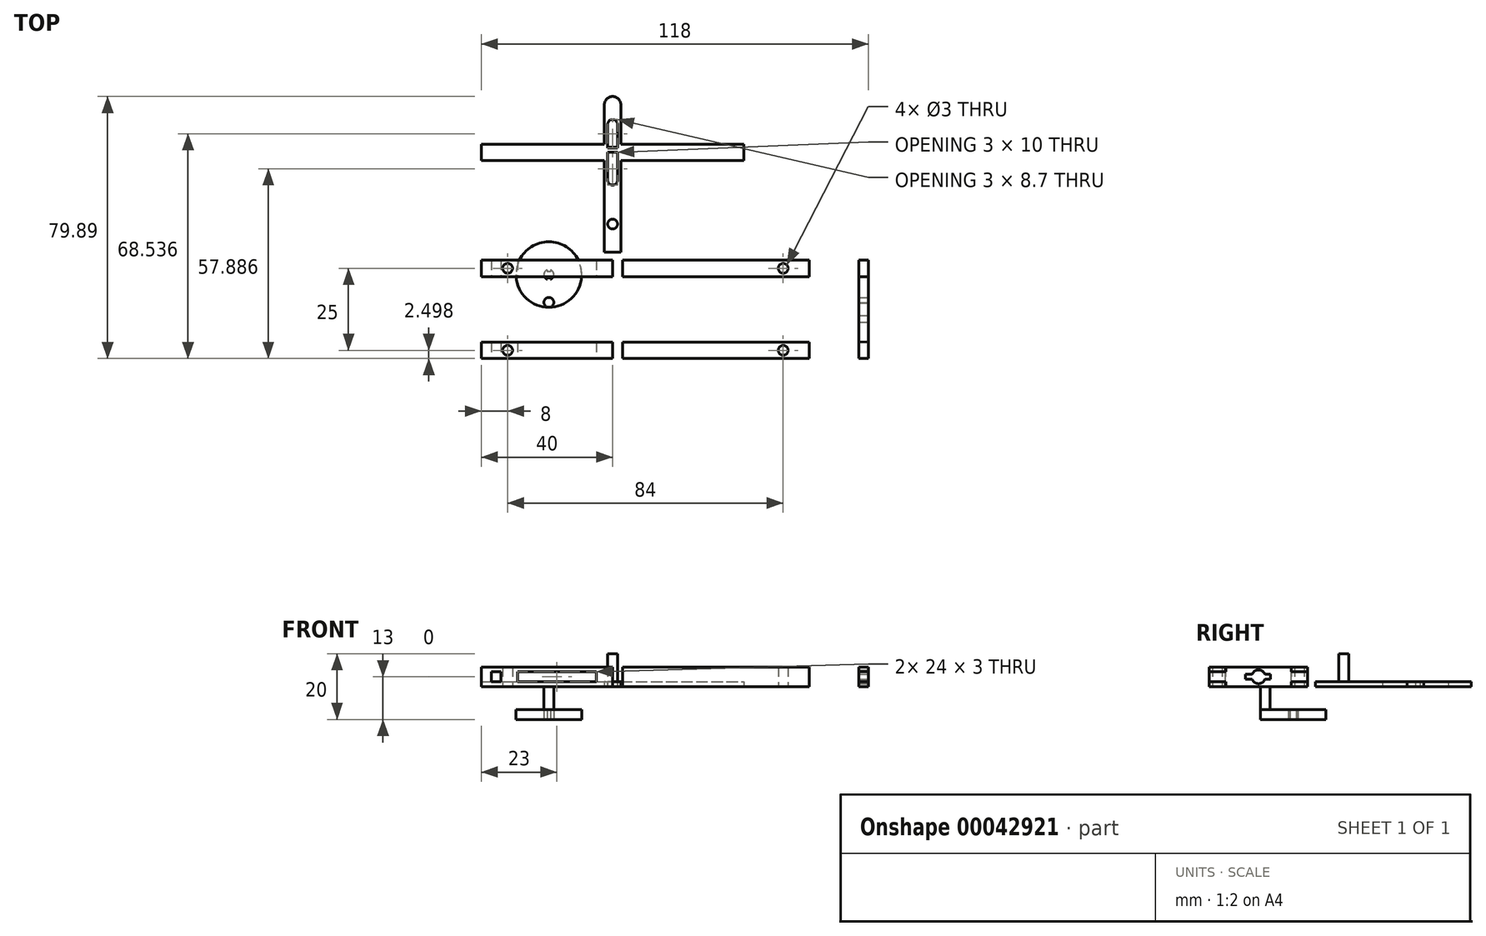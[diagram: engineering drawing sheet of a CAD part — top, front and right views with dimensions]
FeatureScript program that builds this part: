
annotation { "Feature Type Name" : "Feature", "Feature Type Description" : "" }
export const myFeature = defineFeature(function(context is Context, id is Id, definition is map)
    precondition{}
    {
        {
            var Q0;
            Q0=qCreatedBy(makeId("Top.planeOp"),FACE);
            var sketch = newSketch(context, id + "F0", { "sketchPlane" : qUnion([Q0])});
            skLineSegment(sketch, "E0.bottom", {"start": v(-50, 54.04) * mm, "end": v(50, 54.04) * mm});
            skLineSegment(sketch, "E0.top", {"start": v(-50, 49.04) * mm, "end": v(50, 49.04) * mm});
            skLineSegment(sketch, "E0.left", {"start": v(-50, 54.04) * mm, "end": v(-50, 49.04) * mm});
            skLineSegment(sketch, "E0.right", {"start": v(50, 54.04) * mm, "end": v(50, 49.04) * mm});
            skLineSegment(sketch, "E1.bottom", {"start": v(-50, 29.04) * mm, "end": v(50, 29.04) * mm});
            skLineSegment(sketch, "E1.top", {"start": v(-50, 24.04) * mm, "end": v(50, 24.04) * mm});
            skLineSegment(sketch, "E1.left", {"start": v(-50, 29.04) * mm, "end": v(-50, 24.04) * mm});
            skLineSegment(sketch, "E1.right", {"start": v(50, 29.04) * mm, "end": v(50, 24.04) * mm});
            skLineSegment(sketch, "E2", {"start": v(-50, 51.54) * mm, "end": v(50, 51.54) * mm, "construction": true});
            skLineSegment(sketch, "E3", {"start": v(-50, 26.54) * mm, "end": v(50, 26.54) * mm, "construction": true});
            skLineSegment(sketch, "E4", {"start": v(-42, 54.04) * mm, "end": v(-42, 49.04) * mm, "construction": true});
            skLineSegment(sketch, "E5", {"start": v(-42, 29.04) * mm, "end": v(-42, 24.04) * mm, "construction": true});
            skLineSegment(sketch, "E6", {"start": v(42, 29.04) * mm, "end": v(42, 24.04) * mm, "construction": true});
            skLineSegment(sketch, "E7", {"start": v(42, 49.04) * mm, "end": v(42, 54.04) * mm, "construction": true});
            skLineSegment(sketch, "E8", {"start": v(-50, 72.94) * mm, "end": v(-50, -39.34) * mm, "construction": true});
            skCircle(sketch, "E9", {"center": v(-42, 51.54) * mm, "radius": 1.5 * mm});
            skCircle(sketch, "E10", {"center": v(-42, 26.54) * mm, "radius": 1.5 * mm});
            skCircle(sketch, "E11", {"center": v(42, 26.54) * mm, "radius": 1.5 * mm});
            skCircle(sketch, "E12", {"center": v(42, 51.54) * mm, "radius": 1.5 * mm});
            skLineSegment(sketch, "E13.bottom", {"start": v(65, 54.04) * mm, "end": v(68, 54.04) * mm});
            skLineSegment(sketch, "E13.top", {"start": v(65, 24.04) * mm, "end": v(68, 24.04) * mm});
            skLineSegment(sketch, "E13.left", {"start": v(65, 54.04) * mm, "end": v(65, 24.04) * mm});
            skLineSegment(sketch, "E13.right", {"start": v(68, 54.04) * mm, "end": v(68, 24.04) * mm});
            skLineSegment(sketch, "E14", {"start": v(65, 49.04) * mm, "end": v(68, 49.04) * mm});
            skLineSegment(sketch, "E15", {"start": v(65, 29.04) * mm, "end": v(68, 29.17) * mm});
            skLineSegment(sketch, "E16", {"start": v(50, 24.04) * mm, "end": v(81.81, 24.04) * mm, "construction": true});
            skLineSegment(sketch, "E17", {"start": v(50, 54.04) * mm, "end": v(83.42, 54.04) * mm, "construction": true});
            skLineSegment(sketch, "E18.bottom", {"start": v(-10, 54.04) * mm, "end": v(-7, 54.04) * mm});
            skLineSegment(sketch, "E18.top", {"start": v(-10, 49.04) * mm, "end": v(-7, 49.04) * mm});
            skLineSegment(sketch, "E18.left", {"start": v(-10, 54.04) * mm, "end": v(-10, 49.04) * mm});
            skLineSegment(sketch, "E18.right", {"start": v(-7, 54.04) * mm, "end": v(-7, 49.04) * mm});
            skPoint(sketch, "E19.oppositeSnap0", {"position": v(-7, 51.54) * mm});
            skLineSegment(sketch, "E19.bottom", {"start": v(-10, 29.04) * mm, "end": v(-7, 29.04) * mm});
            skLineSegment(sketch, "E19.top", {"start": v(-10, 24.04) * mm, "end": v(-7, 24.04) * mm});
            skLineSegment(sketch, "E19.left", {"start": v(-10, 29.04) * mm, "end": v(-10, 24.04) * mm});
            skLineSegment(sketch, "E19.right", {"start": v(-7, 29.04) * mm, "end": v(-7, 24.04) * mm});
            skLineSegment(sketch, "E20.bottom", {"start": v(-50, 89.43) * mm, "end": v(30, 89.43) * mm});
            skLineSegment(sketch, "E20.top", {"start": v(-50, 84.43) * mm, "end": v(30, 84.43) * mm});
            skLineSegment(sketch, "E20.left", {"start": v(-50, 89.43) * mm, "end": v(-50, 84.43) * mm});
            skLineSegment(sketch, "E20.right", {"start": v(30, 89.43) * mm, "end": v(30, 84.43) * mm});
            skLineSegment(sketch, "E21.bottom", {"start": v(-12.5, 101.43) * mm, "end": v(-7.5, 101.43) * mm});
            skLineSegment(sketch, "E21.top", {"start": v(-12.5, 56.43) * mm, "end": v(-7.5, 56.43) * mm});
            skLineSegment(sketch, "E21.left", {"start": v(-12.5, 101.43) * mm, "end": v(-12.5, 56.43) * mm});
            skLineSegment(sketch, "E21.right", {"start": v(-7.5, 101.43) * mm, "end": v(-7.5, 56.43) * mm});
            skCircle(sketch, "E22", {"center": v(-10, 65.05) * mm, "radius": 1.5 * mm});
            skPoint(sketch, "E22.centerSnap0", {"position": v(-10, 56.43) * mm});
            skLineSegment(sketch, "E23.bottom", {"start": v(-11.5, 95.43) * mm, "end": v(-8.5, 95.43) * mm});
            skLineSegment(sketch, "E23.top", {"start": v(-11.5, 78.43) * mm, "end": v(-8.5, 78.43) * mm});
            skLineSegment(sketch, "E23.left", {"start": v(-11.5, 95.43) * mm, "end": v(-11.5, 78.43) * mm});
            skLineSegment(sketch, "E23.right", {"start": v(-8.5, 95.43) * mm, "end": v(-8.5, 78.43) * mm});
            skArc(sketch, "E24", {"start": v(-8.5, 95.43) * mm, "mid": v(-10, 96.93) * mm, "end": v(-11.5, 95.43) * mm});
            skArc(sketch, "E25", {"start": v(-11.5, 78.43) * mm, "mid": v(-10, 76.93) * mm, "end": v(-8.5, 78.43) * mm});
            skArc(sketch, "E26", {"start": v(-7.5, 101.43) * mm, "mid": v(-10, 103.93) * mm, "end": v(-12.5, 101.43) * mm});
            skLineSegment(sketch, "E27", {"start": v(0, -31.19) * mm, "end": v(0, 115.5) * mm, "construction": true});
            skLineSegment(sketch, "E28", {"start": v(-10, 56.43) * mm, "end": v(-10, 101.43) * mm, "construction": true});
            skCircle(sketch, "E29", {"center": v(-10, 86.93) * mm, "radius": 10 * mm});
            skCircle(sketch, "E30", {"center": v(-10, 95.43) * mm, "radius": 1.5 * mm});
            skLineSegment(sketch, "E31", {"start": v(-50, 86.93) * mm, "end": v(30, 86.93) * mm, "construction": true});
            skSolve(sketch);
        }
        {
            var Q0;
            {var subQ2=sQuery(id+"F0.wireOp",EDGE,"E0.left");Q0=makeQuery(id+"F0.imprint","IMPRINT",FACE,{"disambiguationData":[TD([[makeQuery(id+"F0.imprint","IMPRINT",EDGE,{"derivedFrom":subQ2}),1.0]])]});}
            var Q1;
            Q1=makeQuery(id+"F0.imprint","IMPRINT",FACE,{"disambiguationData":[TD([[makeQuery(id+"F0.imprint","IMPRINT",EDGE,{"derivedFrom":sQuery(id+"F0.wireOp",EDGE,"E18.bottom")}),-1.0]])]});
            var Q2;
            {var subQ2=sQuery(id+"F0.wireOp",EDGE,"E0.right");Q2=makeQuery(id+"F0.imprint","IMPRINT",FACE,{"disambiguationData":[TD([[makeQuery(id+"F0.imprint","IMPRINT",EDGE,{"derivedFrom":subQ2}),-1.0]])]});}
            var Q3;
            {var subQ2=sQuery(id+"F0.wireOp",EDGE,"E1.left");Q3=makeQuery(id+"F0.imprint","IMPRINT",FACE,{"disambiguationData":[TD([[makeQuery(id+"F0.imprint","IMPRINT",EDGE,{"derivedFrom":subQ2}),1.0]])]});}
            var Q4;
            Q4=makeQuery(id+"F0.imprint","IMPRINT",FACE,{"disambiguationData":[TD([[makeQuery(id+"F0.imprint","IMPRINT",EDGE,{"derivedFrom":sQuery(id+"F0.wireOp",EDGE,"E19.bottom")}),-1.0]])]});
            var Q5;
            {var subQ2=sQuery(id+"F0.wireOp",EDGE,"E1.right");Q5=makeQuery(id+"F0.imprint","IMPRINT",FACE,{"disambiguationData":[TD([[makeQuery(id+"F0.imprint","IMPRINT",EDGE,{"derivedFrom":subQ2}),-1.0]])]});}
            extrude(context, id + "F1", {"entities" : qUnion([Q0, Q1, Q2, Q3, Q4, Q5]), "depth" : 6 * mm});
        }
        {
            var Q0;
            {var subQ2=sQuery(id+"F0.wireOp",EDGE,"E13.bottom");Q0=makeQuery(id+"F0.imprint","IMPRINT",FACE,{"disambiguationData":[TD([[makeQuery(id+"F0.imprint","IMPRINT",EDGE,{"derivedFrom":subQ2}),-1.0]])]});}
            var Q1;
            {var subQ1=sQuery(id+"F0.wireOp",EDGE,"E14");Q1=makeQuery(id+"F0.imprint","IMPRINT",FACE,{"disambiguationData":[TD([[makeQuery(id+"F0.imprint","IMPRINT",EDGE,{"derivedFrom":subQ1}),-1.0]])]});}
            var Q2;
            {var subQ2=sQuery(id+"F0.wireOp",EDGE,"E13.top");Q2=makeQuery(id+"F0.imprint","IMPRINT",FACE,{"disambiguationData":[TD([[makeQuery(id+"F0.imprint","IMPRINT",EDGE,{"derivedFrom":subQ2}),1.0]])]});}
            extrude(context, id + "F2", {"entities" : qUnion([Q0, Q1, Q2]), "depth" : 4.5 * mm, "hasSecondDirection" : true, "secondDirectionOppositeDirection" : false, "secondDirectionDepth" : 1.5 * mm});
        }
        {
            var Q0;
            {var subQ1=sQuery(id+"F0.wireOp",EDGE,"E14");Q0=makeQuery(id+"F0.imprint","IMPRINT",FACE,{"disambiguationData":[TD([[makeQuery(id+"F0.imprint","IMPRINT",EDGE,{"derivedFrom":subQ1}),-1.0]])]});}
            extrude(context, id + "F3", {"entities" : qUnion([Q0]), "operationType" : NewBodyOperationType.ADD, "depth" : 6 * mm});
        }
        {
            var Q0;
            {var subQ0=sQuery(id+"F0.wireOp",EDGE,"E13.right");Q0=makeQuery(id+"F3.boolean.opBoolean","MERGE",FACE,{"derivedFrom":[makeQuery(id+"F2.opExtrude","SWEPT_FACE",FACE,{"disambiguationData":[OSD([subQ0])]}),makeQuery(id+"F3.opExtrude","SWEPT_FACE",FACE,{"disambiguationData":[OSD([subQ0])]})]});}
            var sketch = newSketch(context, id + "F4", { "sketchPlane" : qUnion([Q0])});
            skCircle(sketch, "E32", {"center": v(39.1, 3) * mm, "radius": 2.1 * mm});
            skPoint(sketch, "E32.centerSnap0", {"position": v(54.04, 3) * mm});
            skPoint(sketch, "E32.centerSnap1", {"position": v(39.1, 6) * mm});
            skLineSegment(sketch, "E33.bottom", {"start": v(35.1, 3.81) * mm, "end": v(42.69, 3.81) * mm});
            skLineSegment(sketch, "E33.top", {"start": v(35.1, 2.27) * mm, "end": v(42.69, 2.27) * mm});
            skLineSegment(sketch, "E33.left", {"start": v(35.1, 3.81) * mm, "end": v(35.1, 2.27) * mm});
            skLineSegment(sketch, "E33.right", {"start": v(42.69, 3.81) * mm, "end": v(42.69, 2.27) * mm});
            skSolve(sketch);
        }
        {
            var Q0;
            {var subQ0=sQuery(id+"F4.wireOp",EDGE,"E33.bottom");var subQ1=sQuery(id+"F4.wireOp",EDGE,"E32");var subQ3=makeQuery(id+"F4.imprint","INTERSECT",VERTEX,{"disambiguationData":[OD(0.0)],"derivedFrom":[subQ1,subQ0]});Q0=makeQuery(id+"F4.imprint","IMPRINT",FACE,{"disambiguationData":[TD([[makeQuery(id+"F4.imprint","IMPRINT",EDGE,{"disambiguationData":[TD([[subQ3,1.0]])],"derivedFrom":subQ1}),1.0]])]});}
            var Q1;
            {var subQ1=sQuery(id+"F4.wireOp",EDGE,"E32");var subQ4=sQuery(id+"F4.wireOp",EDGE,"E33.bottom");var subQ6=makeQuery(id+"F4.imprint","INTERSECT",VERTEX,{"disambiguationData":[OD(0.0)],"derivedFrom":[subQ1,subQ4]});Q1=makeQuery(id+"F4.imprint","IMPRINT",FACE,{"disambiguationData":[TD([[makeQuery(id+"F4.imprint","IMPRINT",EDGE,{"disambiguationData":[TD([[subQ6,-1.0]])],"derivedFrom":subQ1}),1.0]])]});}
            var Q2;
            {var subQ0=sQuery(id+"F4.wireOp",EDGE,"E33.right");Q2=makeQuery(id+"F4.imprint","IMPRINT",FACE,{"disambiguationData":[TD([[makeQuery(id+"F4.imprint","IMPRINT",EDGE,{"derivedFrom":subQ0}),-1.0]])]});}
            var Q3;
            {var subQ0=sQuery(id+"F4.wireOp",EDGE,"E33.top");var subQ1=sQuery(id+"F4.wireOp",EDGE,"E32");var subQ3=makeQuery(id+"F4.imprint","INTERSECT",VERTEX,{"disambiguationData":[OD(0.0)],"derivedFrom":[subQ1,subQ0]});Q3=makeQuery(id+"F4.imprint","IMPRINT",FACE,{"disambiguationData":[TD([[makeQuery(id+"F4.imprint","IMPRINT",EDGE,{"disambiguationData":[TD([[subQ3,-1.0]])],"derivedFrom":subQ1}),1.0]])]});}
            var Q4;
            {var subQ0=sQuery(id+"F4.wireOp",EDGE,"E33.left");Q4=makeQuery(id+"F4.imprint","IMPRINT",FACE,{"disambiguationData":[TD([[makeQuery(id+"F4.imprint","IMPRINT",EDGE,{"derivedFrom":subQ0}),1.0]])]});}
            extrude(context, id + "F5", {"entities" : qUnion([Q0, Q1, Q2, Q3, Q4]), "operationType" : NewBodyOperationType.REMOVE, "endBound" : BoundingType.THROUGH_ALL, "oppositeDirection" : true, "depth" : 3 * mm});
        }
        {
            var Q0;
            Q0=makeQuery(id+"F1.opExtrude","SWEPT_FACE",FACE,{"disambiguationData":[OSD([sQuery(id+"F0.wireOp",EDGE,"E1.top"),sQuery(id+"F0.wireOp",EDGE,"E19.top")])]});
            var sketch = newSketch(context, id + "F6", { "sketchPlane" : qUnion([Q0])});
            skLineSegment(sketch, "E34.bottom", {"start": v(-7, 4.5) * mm, "end": v(-10, 4.5) * mm});
            skLineSegment(sketch, "E34.top", {"start": v(-7, 1.5) * mm, "end": v(-10, 1.5) * mm});
            skLineSegment(sketch, "E34.left", {"start": v(-7, 1.5) * mm, "end": v(-7, 4.5) * mm});
            skLineSegment(sketch, "E34.right", {"start": v(-10, 1.5) * mm, "end": v(-10, 4.5) * mm});
            skLineSegment(sketch, "E35", {"start": v(-7, 1.5) * mm, "end": v(-7, 4.5) * mm, "construction": true});
            skPoint(sketch, "E36.orphan", {"position": v(-7, 6) * mm});
            skPoint(sketch, "E37.orphan", {"position": v(-10, 6) * mm});
            skPoint(sketch, "E38.orphan", {"position": v(-10, 0) * mm});
            skLineSegment(sketch, "E39.bottom", {"start": v(-47, 4.5) * mm, "end": v(-44, 4.5) * mm});
            skLineSegment(sketch, "E39.top", {"start": v(-47, 1.5) * mm, "end": v(-44, 1.5) * mm});
            skLineSegment(sketch, "E39.left", {"start": v(-47, 4.5) * mm, "end": v(-47, 1.5) * mm});
            skLineSegment(sketch, "E39.right", {"start": v(-44, 4.5) * mm, "end": v(-44, 1.5) * mm});
            skLineSegment(sketch, "E40.bottom", {"start": v(-39, 4.5) * mm, "end": v(-15, 4.5) * mm});
            skLineSegment(sketch, "E40.top", {"start": v(-39, 1.5) * mm, "end": v(-15, 1.5) * mm});
            skLineSegment(sketch, "E40.left", {"start": v(-39, 4.5) * mm, "end": v(-39, 1.5) * mm});
            skLineSegment(sketch, "E40.right", {"start": v(-15, 4.5) * mm, "end": v(-15, 1.5) * mm});
            skSolve(sketch);
        }
        {
            var Q0;
            {var subQ2=sQuery(id+"F6.wireOp",EDGE,"E34.bottom");Q0=makeQuery(id+"F6.imprint","IMPRINT",FACE,{"disambiguationData":[TD([[makeQuery(id+"F6.imprint","IMPRINT",EDGE,{"derivedFrom":subQ2}),1.0]])]});}
            var Q1;
            Q1=makeQuery(id+"F6.imprint","IMPRINT",FACE,{"disambiguationData":[TD([[makeQuery(id+"F6.imprint","IMPRINT",EDGE,{"derivedFrom":sQuery(id+"F6.wireOp",EDGE,"E39.bottom")}),-1.0]])]});
            var Q2;
            Q2=makeQuery(id+"F6.imprint","IMPRINT",FACE,{"disambiguationData":[TD([[makeQuery(id+"F6.imprint","IMPRINT",EDGE,{"derivedFrom":sQuery(id+"F6.wireOp",EDGE,"E40.bottom")}),-1.0]])]});
            extrude(context, id + "F7", {"entities" : qUnion([Q0, Q1, Q2]), "operationType" : NewBodyOperationType.REMOVE, "endBound" : BoundingType.THROUGH_ALL, "oppositeDirection" : true, "depth" : 25 * mm});
        }
        {
            var Q0;
            {var subQ0=sQuery(id+"F0.wireOp",EDGE,"E20.right");Q0=makeQuery(id+"F0.imprint","IMPRINT",FACE,{"disambiguationData":[TD([[makeQuery(id+"F0.imprint","IMPRINT",EDGE,{"derivedFrom":subQ0}),-1.0]])]});}
            var Q1;
            {var subQ0=sQuery(id+"F0.wireOp",EDGE,"E20.left");Q1=makeQuery(id+"F0.imprint","IMPRINT",FACE,{"disambiguationData":[TD([[makeQuery(id+"F0.imprint","IMPRINT",EDGE,{"derivedFrom":subQ0}),1.0]])]});}
            var Q2;
            Q2=makeQuery(id+"F0.imprint","IMPRINT",FACE,{"disambiguationData":[TD([[makeQuery(id+"F0.imprint","IMPRINT",EDGE,{"derivedFrom":sQuery(id+"F0.wireOp",EDGE,"E21.bottom")}),1.0]])]});
            var Q3;
            {var subQ7=sQuery(id+"F0.wireOp",EDGE,"E21.bottom");Q3=makeQuery(id+"F0.imprint","IMPRINT",FACE,{"disambiguationData":[TD([[makeQuery(id+"F0.imprint","IMPRINT",EDGE,{"derivedFrom":subQ7}),-1.0]])]});}
            var Q4;
            {var subQ7=sQuery(id+"F0.wireOp",EDGE,"E21.top");Q4=makeQuery(id+"F0.imprint","IMPRINT",FACE,{"disambiguationData":[TD([[makeQuery(id+"F0.imprint","IMPRINT",EDGE,{"derivedFrom":subQ7}),1.0]])]});}
            var Q5;
            {var subQ3=sQuery(id+"F0.wireOp",EDGE,"E20.bottom");var subQ5=sQuery(id+"F0.wireOp",EDGE,"E21.left");var subQ7=makeQuery(id+"F0.imprint","INTERSECT",VERTEX,{"derivedFrom":[subQ3,subQ5]});Q5=makeQuery(id+"F0.imprint","IMPRINT",FACE,{"disambiguationData":[TD([[makeQuery(id+"F0.imprint","IMPRINT",EDGE,{"disambiguationData":[TD([[subQ7,-1.0]])],"derivedFrom":subQ3}),-1.0]])]});}
            var Q6;
            {var subQ3=sQuery(id+"F0.wireOp",EDGE,"E20.bottom");var subQ5=sQuery(id+"F0.wireOp",EDGE,"E21.right");var subQ7=makeQuery(id+"F0.imprint","INTERSECT",VERTEX,{"derivedFrom":[subQ3,subQ5]});Q6=makeQuery(id+"F0.imprint","IMPRINT",FACE,{"disambiguationData":[TD([[makeQuery(id+"F0.imprint","IMPRINT",EDGE,{"disambiguationData":[TD([[subQ7,1.0]])],"derivedFrom":subQ3}),-1.0]])]});}
            var Q7;
            {var subQ3=sQuery(id+"F0.wireOp",EDGE,"E20.bottom");var subQ5=sQuery(id+"F0.wireOp",EDGE,"E29");var subQ7=makeQuery(id+"F0.imprint","INTERSECT",VERTEX,{"disambiguationData":[OD(0.0)],"derivedFrom":[subQ3,subQ5]});Q7=makeQuery(id+"F0.imprint","IMPRINT",FACE,{"disambiguationData":[TD([[makeQuery(id+"F0.imprint","IMPRINT",EDGE,{"disambiguationData":[TD([[subQ7,-1.0]])],"derivedFrom":subQ3}),-1.0]])]});}
            var Q8;
            {var subQ3=sQuery(id+"F0.wireOp",EDGE,"E20.bottom");var subQ5=sQuery(id+"F0.wireOp",EDGE,"E29");var subQ7=makeQuery(id+"F0.imprint","INTERSECT",VERTEX,{"disambiguationData":[OD(1.0)],"derivedFrom":[subQ3,subQ5]});Q8=makeQuery(id+"F0.imprint","IMPRINT",FACE,{"disambiguationData":[TD([[makeQuery(id+"F0.imprint","IMPRINT",EDGE,{"disambiguationData":[TD([[subQ7,1.0]])],"derivedFrom":subQ3}),-1.0]])]});}
            var Q9;
            {var subQ5=sQuery(id+"F0.wireOp",EDGE,"E20.bottom");var subQ7=sQuery(id+"F0.wireOp",EDGE,"E21.left");var subQ8=makeQuery(id+"F0.imprint","INTERSECT",VERTEX,{"derivedFrom":[subQ5,subQ7]});Q9=makeQuery(id+"F0.imprint","IMPRINT",FACE,{"disambiguationData":[TD([[makeQuery(id+"F0.imprint","IMPRINT",EDGE,{"disambiguationData":[TD([[subQ8,-1.0]])],"derivedFrom":subQ5}),1.0]])]});}
            var Q10;
            {var subQ3=sQuery(id+"F0.wireOp",EDGE,"E23.right");var subQ5=sQuery(id+"F0.wireOp",EDGE,"E20.bottom");var subQ8=makeQuery(id+"F0.imprint","INTERSECT",VERTEX,{"derivedFrom":[subQ5,subQ3]});Q10=makeQuery(id+"F0.imprint","IMPRINT",FACE,{"disambiguationData":[TD([[makeQuery(id+"F0.imprint","IMPRINT",EDGE,{"disambiguationData":[TD([[subQ8,-1.0]])],"derivedFrom":subQ5}),1.0]])]});}
            var Q11;
            {var subQ5=sQuery(id+"F0.wireOp",EDGE,"E20.top");var subQ7=sQuery(id+"F0.wireOp",EDGE,"E23.right");var subQ8=makeQuery(id+"F0.imprint","INTERSECT",VERTEX,{"derivedFrom":[subQ5,subQ7]});Q11=makeQuery(id+"F0.imprint","IMPRINT",FACE,{"disambiguationData":[TD([[makeQuery(id+"F0.imprint","IMPRINT",EDGE,{"disambiguationData":[TD([[subQ8,-1.0]])],"derivedFrom":subQ5}),-1.0]])]});}
            var Q12;
            {var subQ0=sQuery(id+"F0.wireOp",EDGE,"E20.top");var subQ3=sQuery(id+"F0.wireOp",EDGE,"E21.left");var subQ4=makeQuery(id+"F0.imprint","INTERSECT",VERTEX,{"derivedFrom":[subQ0,subQ3]});Q12=makeQuery(id+"F0.imprint","IMPRINT",FACE,{"disambiguationData":[TD([[makeQuery(id+"F0.imprint","IMPRINT",EDGE,{"disambiguationData":[TD([[subQ4,-1.0]])],"derivedFrom":subQ0}),-1.0]])]});}
            extrude(context, id + "F8", {"entities" : qUnion([Q0, Q1, Q2, Q3, Q4, Q5, Q6, Q7, Q8, Q9, Q10, Q11, Q12]), "operationType" : NewBodyOperationType.ADD, "depth" : 1.5 * mm});
        }
        {
            var Q0;
            Q0=makeQuery(id+"F0.imprint","IMPRINT",FACE,{"disambiguationData":[TD([[makeQuery(id+"F0.imprint","IMPRINT",EDGE,{"derivedFrom":sQuery(id+"F0.wireOp",EDGE,"E22")}),1.0]])]});
            extrude(context, id + "F9", {"entities" : qUnion([Q0]), "operationType" : NewBodyOperationType.ADD, "depth" : 10 * mm});
        }
        {
            var Q0;
            Q0=makeQuery(id+"F8.opExtrude","SWEPT_FACE",FACE,{"disambiguationData":[OSD([sQuery(id+"F0.wireOp",EDGE,"E20.right")])]});
            var sketch = newSketch(context, id + "F10", { "sketchPlane" : qUnion([Q0])});
            skLineSegment(sketch, "E41", {"start": v(84.43, 0.75) * mm, "end": v(89.43, 0.75) * mm, "construction": true});
            skLineSegment(sketch, "E42", {"start": v(86.93, 1.5) * mm, "end": v(86.93, 0) * mm});
            skCircle(sketch, "E43", {"center": v(86.93, 0.75) * mm, "radius": 1.5 * mm});
            skSolve(sketch);
        }
        {
            var Q0;
            {var subQ0=makeQuery(id+"F8.opExtrude","CAP_EDGE",EDGE,{"disambiguationData":[OSD([sQuery(id+"F0.wireOp",EDGE,"E20.right")])],"isStart":false});var subQ1=sQuery(id+"F10.wireOp",EDGE,"E43");var subQ4=makeQuery(id+"F10.imprint","INTERSECT",VERTEX,{"disambiguationData":[OD(0.0)],"derivedFrom":[subQ0,subQ1]});Q0=makeQuery(id+"F10.imprint","IMPRINT",FACE,{"disambiguationData":[TD([[makeQuery(id+"F10.imprint","IMPRINT",EDGE,{"disambiguationData":[TD([[subQ4,1.0]])],"derivedFrom":subQ1}),1.0]])]});}
            var Q1;
            {var subQ0=makeQuery(id+"F8.opExtrude","CAP_EDGE",EDGE,{"disambiguationData":[OSD([sQuery(id+"F0.wireOp",EDGE,"E20.right")])],"isStart":true});var subQ1=sQuery(id+"F10.wireOp",EDGE,"E43");var subQ4=makeQuery(id+"F10.imprint","INTERSECT",VERTEX,{"disambiguationData":[OD(0.0)],"derivedFrom":[subQ0,subQ1]});Q1=makeQuery(id+"F10.imprint","IMPRINT",FACE,{"disambiguationData":[TD([[makeQuery(id+"F10.imprint","IMPRINT",EDGE,{"disambiguationData":[TD([[subQ4,-1.0]])],"derivedFrom":subQ1}),1.0]])]});}
            extrude(context, id + "F11", {"entities" : qUnion([Q0, Q1]), "operationType" : NewBodyOperationType.ADD, "oppositeDirection" : true, "depth" : 60 * mm});
        }
        {
            var Q0;
            {var subQ0=sQuery(id+"F0.wireOp",EDGE,"E29");var subQ3=sQuery(id+"F0.wireOp",EDGE,"E20.bottom");var subQ4=makeQuery(id+"F0.imprint","INTERSECT",VERTEX,{"disambiguationData":[OD(1.0)],"derivedFrom":[subQ3,subQ0]});Q0=makeQuery(id+"F0.imprint","IMPRINT",FACE,{"disambiguationData":[TD([[makeQuery(id+"F0.imprint","IMPRINT",EDGE,{"disambiguationData":[TD([[subQ4,1.0]])],"derivedFrom":subQ3}),1.0]])]});}
            cPlane(context, id + "F12", {"entities" : qUnion([Q0]), "cplaneType" : CPlaneType.OFFSET, "offset" : 10 * mm, "oppositeDirection" : true, "width" : 150 * mm, "height" : 150 * mm});
        }
        {
            var Q0;
            Q0=qCreatedBy(id+"F12.planeOp",FACE);
            var sketch = newSketch(context, id + "F13", { "sketchPlane" : qUnion([Q0])});
            skPoint(sketch, "E44.centerSnap0", {"position": v(-29.43, 19.15) * mm});
            skLineSegment(sketch, "E45.left", {"start": v(-30.93, 58.15) * mm, "end": v(-30.93, 41.15) * mm});
            skLineSegment(sketch, "E45.right", {"start": v(-27.93, 58.15) * mm, "end": v(-27.93, 41.15) * mm});
            skArc(sketch, "E46", {"start": v(-27.93, 58.15) * mm, "mid": v(-29.43, 59.65) * mm, "end": v(-30.93, 58.15) * mm});
            skArc(sketch, "E47", {"start": v(-30.93, 41.15) * mm, "mid": v(-29.43, 39.65) * mm, "end": v(-27.93, 41.15) * mm});
            skLineSegment(sketch, "E48", {"start": v(-29.43, 19.15) * mm, "end": v(-29.43, 64.15) * mm, "construction": true});
            skCircle(sketch, "E49", {"center": v(-29.43, 49.65) * mm, "radius": 10 * mm});
            skCircle(sketch, "E50", {"center": v(-29.43, 49.65) * mm, "radius": 1.5 * mm});
            skLineSegment(sketch, "E51.bottom", {"start": v(-29.93, 48.23) * mm, "end": v(-28.93, 48.23) * mm});
            skLineSegment(sketch, "E51.top", {"start": v(-29.93, 48.73) * mm, "end": v(-28.93, 48.73) * mm});
            skLineSegment(sketch, "E51.left", {"start": v(-29.93, 48.23) * mm, "end": v(-29.93, 48.73) * mm});
            skLineSegment(sketch, "E51.right", {"start": v(-28.93, 48.23) * mm, "end": v(-28.93, 48.73) * mm});
            skLineSegment(sketch, "E52.bottom", {"start": v(-28.93, 51.06) * mm, "end": v(-29.93, 51.06) * mm});
            skLineSegment(sketch, "E52.top", {"start": v(-28.93, 50.56) * mm, "end": v(-29.93, 50.56) * mm});
            skLineSegment(sketch, "E52.left", {"start": v(-28.93, 51.06) * mm, "end": v(-28.93, 50.56) * mm});
            skLineSegment(sketch, "E52.right", {"start": v(-29.93, 51.06) * mm, "end": v(-29.93, 50.56) * mm});
            skArc(sketch, "E53", {"start": v(-27.93, 41.15) * mm, "mid": v(-29.43, 42.65) * mm, "end": v(-30.93, 41.15) * mm});
            skLineSegment(sketch, "E54", {"start": v(-27.93, 41.15) * mm, "end": v(-30.93, 41.15) * mm, "construction": true});
            skSolve(sketch);
        }
        {
            var Q0;
            {var subQ0=sQuery(id+"F13.wireOp",EDGE,"E46");var subQ3=sQuery(id+"F13.wireOp",EDGE,"E45.right");var subQ4=makeQuery(id+"F13.imprint","INTERSECT",VERTEX,{"derivedFrom":[subQ3,subQ0]});Q0=makeQuery(id+"F13.imprint","IMPRINT",FACE,{"disambiguationData":[TD([[makeQuery(id+"F13.imprint","IMPRINT",EDGE,{"disambiguationData":[TD([[subQ4,-1.0]])],"derivedFrom":subQ3}),1.0]])]});}
            var Q1;
            {var subQ0=sQuery(id+"F13.wireOp",EDGE,"E53");Q1=makeQuery(id+"F13.imprint","IMPRINT",FACE,{"disambiguationData":[TD([[makeQuery(id+"F13.imprint","IMPRINT",EDGE,{"derivedFrom":subQ0}),1.0]])]});}
            var Q2;
            {var subQ0=sQuery(id+"F13.wireOp",EDGE,"E46");var subQ3=sQuery(id+"F13.wireOp",EDGE,"E45.left");var subQ4=makeQuery(id+"F13.imprint","INTERSECT",VERTEX,{"derivedFrom":[subQ3,subQ0]});Q2=makeQuery(id+"F13.imprint","IMPRINT",FACE,{"disambiguationData":[TD([[makeQuery(id+"F13.imprint","IMPRINT",EDGE,{"disambiguationData":[TD([[subQ4,-1.0]])],"derivedFrom":subQ3}),-1.0]])]});}
            var Q3;
            {var subQ8=sQuery(id+"F13.wireOp",EDGE,"E53");Q3=makeQuery(id+"F13.imprint","IMPRINT",FACE,{"disambiguationData":[TD([[makeQuery(id+"F13.imprint","IMPRINT",EDGE,{"derivedFrom":subQ8}),-1.0]])]});}
            var Q4;
            {var subQ1=sQuery(id+"F13.wireOp",EDGE,"E45.left");var subQ8=sQuery(id+"F13.wireOp",EDGE,"E46");var subQ9=makeQuery(id+"F13.imprint","INTERSECT",VERTEX,{"derivedFrom":[subQ1,subQ8]});Q4=makeQuery(id+"F13.imprint","IMPRINT",FACE,{"disambiguationData":[TD([[makeQuery(id+"F13.imprint","IMPRINT",EDGE,{"disambiguationData":[TD([[subQ9,-1.0]])],"derivedFrom":subQ1}),1.0]])]});}
            var Q5;
            Q5=makeQuery(id+"F13.imprint","IMPRINT",FACE,{"disambiguationData":[TD([[makeQuery(id+"F13.imprint","IMPRINT",EDGE,{"derivedFrom":sQuery(id+"F13.wireOp",EDGE,"E52.bottom")}),1.0]])]});
            var Q6;
            {var subQ0=sQuery(id+"F13.wireOp",EDGE,"E52.bottom");Q6=makeQuery(id+"F13.imprint","IMPRINT",FACE,{"disambiguationData":[TD([[makeQuery(id+"F13.imprint","IMPRINT",EDGE,{"derivedFrom":subQ0}),-1.0]])]});}
            var Q7;
            Q7=makeQuery(id+"F13.imprint","IMPRINT",FACE,{"disambiguationData":[TD([[makeQuery(id+"F13.imprint","IMPRINT",EDGE,{"derivedFrom":sQuery(id+"F13.wireOp",EDGE,"E51.bottom")}),1.0]])]});
            var Q8;
            {var subQ0=sQuery(id+"F13.wireOp",EDGE,"E51.bottom");Q8=makeQuery(id+"F13.imprint","IMPRINT",FACE,{"disambiguationData":[TD([[makeQuery(id+"F13.imprint","IMPRINT",EDGE,{"derivedFrom":subQ0}),-1.0]])]});}
            extrude(context, id + "F14", {"entities" : qUnion([Q0, Q1, Q2, Q3, Q4, Q5, Q6, Q7, Q8]), "depth" : 3 * mm});
        }
        {
            var Q0;
            {var subQ0=sQuery(id+"F13.wireOp",EDGE,"E53");Q0=makeQuery(id+"F13.imprint","IMPRINT",FACE,{"disambiguationData":[TD([[makeQuery(id+"F13.imprint","IMPRINT",EDGE,{"derivedFrom":subQ0}),1.0]])]});}
            extrude(context, id + "F15", {"entities" : qUnion([Q0]), "operationType" : NewBodyOperationType.ADD, "depth" : 10 * mm});
        }
    });
